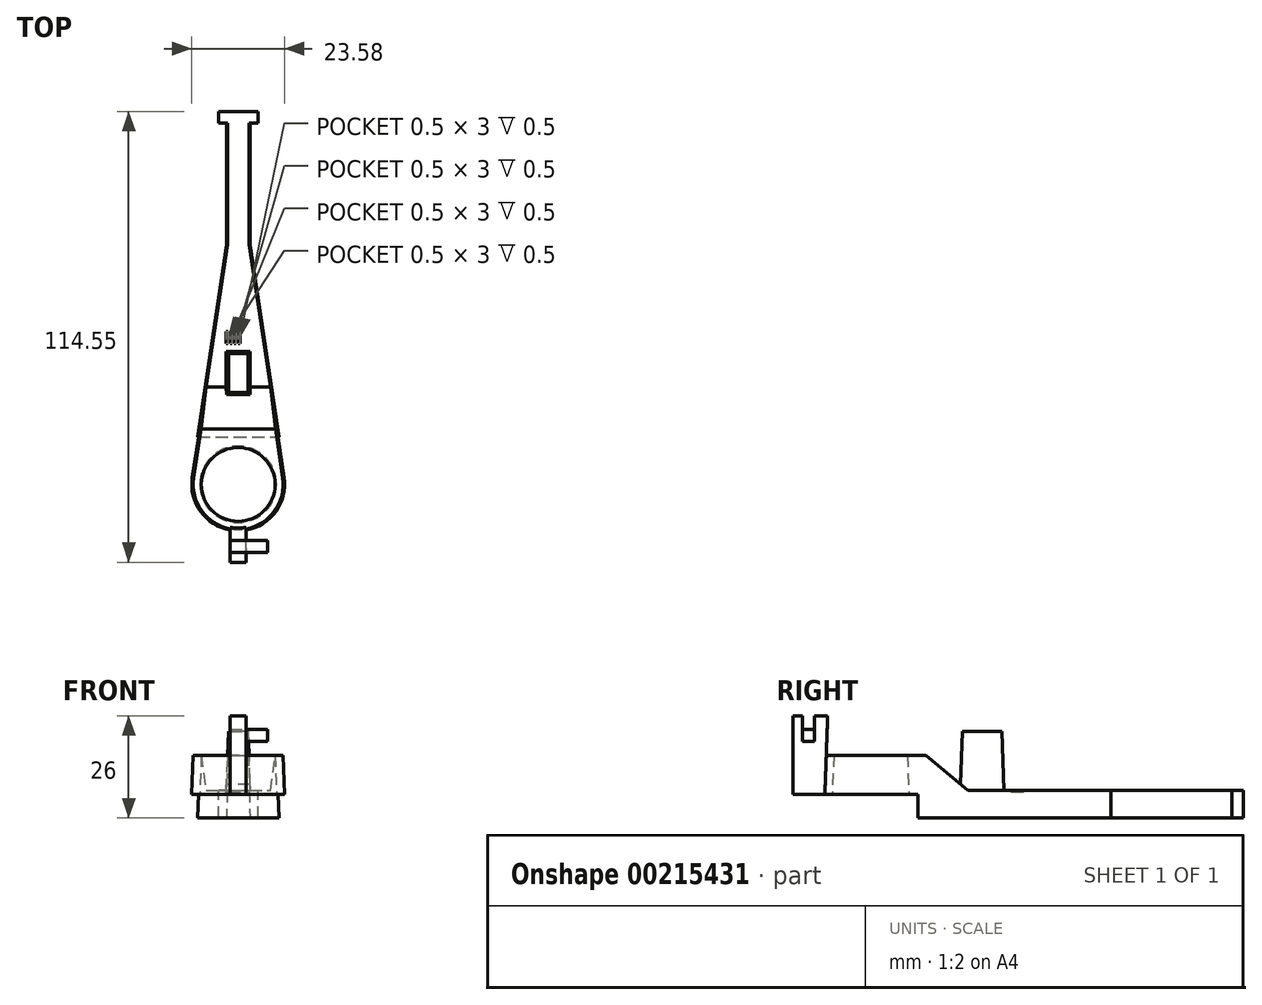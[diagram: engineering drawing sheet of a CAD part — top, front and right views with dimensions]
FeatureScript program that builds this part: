
annotation { "Feature Type Name" : "Feature", "Feature Type Description" : "" }
export const myFeature = defineFeature(function(context is Context, id is Id, definition is map)
    precondition{}
    {
        {
            var Q0;
            Q0=qCreatedBy(makeId("Top.planeOp"),FACE);
            var sketch = newSketch(context, id + "F0", { "sketchPlane" : qUnion([Q0])});
            skCircle(sketch, "E0", {"center": v(0, 0) * mm, "radius": 12 * mm});
            skLineSegment(sketch, "E1", {"start": v(-3, 95) * mm, "end": v(3, 95) * mm});
            skLineSegment(sketch, "E2", {"start": v(0, -12) * mm, "end": v(0, 95) * mm, "construction": true});
            skPoint(sketch, "E3", {"position": v(0, 95) * mm});
            skLineSegment(sketch, "E4", {"start": v(-3, 95) * mm, "end": v(-3, 61) * mm});
            skLineSegment(sketch, "E5", {"start": v(3, 95) * mm, "end": v(3, 61) * mm});
            skLineSegment(sketch, "E6", {"start": v(-3, 61) * mm, "end": v(-11.87, 1.78) * mm});
            skLineSegment(sketch, "E7", {"start": v(3, 61) * mm, "end": v(11.87, 1.78) * mm});
            skSolve(sketch);
        }
        {
            var Q0;
            Q0=qSketchRegion(id+"F0",true);
            extrude(context, id + "F1", {"entities" : qUnion([Q0]), "depth" : 16 * mm, "hasDraft" : true, "draftAngle" : 2 * degree, "draftPullDirection" : true});
        }
        {
            var Q0;
            Q0=qCreatedBy(makeId("Right.planeOp"),FACE);
            cPlane(context, id + "F2", {"entities" : qUnion([Q0]), "cplaneType" : CPlaneType.OFFSET, "offset" : 12 * mm, "width" : 150 * mm, "height" : 150 * mm});
        }
        {
            var Q0;
            Q0=qCreatedBy(id+"F2.planeOp",FACE);
            var sketch = newSketch(context, id + "F3", { "sketchPlane" : qUnion([Q0])});
            skLineSegment(sketch, "E8", {"start": v(94.76, 7) * mm, "end": v(24.76, 7) * mm});
            skLineSegment(sketch, "E9", {"start": v(24.76, 7) * mm, "end": v(14.03, 16) * mm});
            skLineSegment(sketch, "E10", {"start": v(12, 0) * mm, "end": v(12, 6) * mm});
            skLineSegment(sketch, "E11", {"start": v(12, 6) * mm, "end": v(-11.8, 6) * mm});
            skLineSegment(sketch, "E12", {"start": v(12, 0) * mm, "end": v(-12, 0) * mm});
            skLineSegment(sketch, "E13", {"start": v(-12, 0) * mm, "end": v(-11.8, 6) * mm});
            skLineSegment(sketch, "E14", {"start": v(14.03, 16) * mm, "end": v(94.44, 16) * mm});
            skLineSegment(sketch, "E15", {"start": v(94.44, 16) * mm, "end": v(94.76, 7) * mm});
            skSolve(sketch);
        }
        {
            var Q0;
            Q0=qSketchRegion(id+"F3",true);
            extrude(context, id + "F4", {"entities" : qUnion([Q0]), "operationType" : NewBodyOperationType.REMOVE, "endBound" : BoundingType.THROUGH_ALL, "oppositeDirection" : true, "depth" : 25 * mm});
        }
        {
            var Q0;
            Q0=makeQuery(id+"F4.boolean.opBoolean","COPY",FACE,{"derivedFrom":makeQuery(id+"F4.opExtrude","SWEPT_FACE",FACE,{"disambiguationData":[OSD([sQuery(id+"F3.wireOp",EDGE,"E8")])]})});
            cPlane(context, id + "F5", {"entities" : qUnion([Q0]), "cplaneType" : CPlaneType.OFFSET, "offset" : 15 * mm, "width" : 150 * mm, "height" : 150 * mm});
        }
        {
            var Q0;
            Q0=qCreatedBy(id+"F5.planeOp",FACE);
            var sketch = newSketch(context, id + "F6", { "sketchPlane" : qUnion([Q0])});
            skLineSegment(sketch, "E16.bottom", {"start": v(-2.5, 23.3) * mm, "end": v(2.5, 23.3) * mm});
            skLineSegment(sketch, "E16.top", {"start": v(-2.5, 33.3) * mm, "end": v(2.5, 33.3) * mm});
            skLineSegment(sketch, "E16.left", {"start": v(-2.5, 23.3) * mm, "end": v(-2.5, 33.3) * mm});
            skLineSegment(sketch, "E16.right", {"start": v(2.5, 23.3) * mm, "end": v(2.5, 33.3) * mm});
            skPoint(sketch, "E16.middle", {"position": v(0, 28.3) * mm});
            skSolve(sketch);
        }
        {
            var Q0;
            Q0=qSketchRegion(id+"F6",true);
            extrude(context, id + "F7", {"entities" : qUnion([Q0]), "operationType" : NewBodyOperationType.ADD, "endBound" : BoundingType.UP_TO_NEXT, "oppositeDirection" : true, "depth" : 25 * mm, "hasDraft" : true, "draftAngle" : 2 * degree});
        }
        {
            var Q0;
            Q0=makeQuery(id+"F4.boolean.opBoolean","COPY",FACE,{"derivedFrom":makeQuery(id+"F4.opExtrude","SWEPT_FACE",FACE,{"disambiguationData":[OSD([sQuery(id+"F3.wireOp",EDGE,"E11")])]})});
            var sketch = newSketch(context, id + "F8", { "sketchPlane" : qUnion([Q0])});
            skCircle(sketch, "E17", {"center": v(0, 0) * mm, "radius": 9.72 * mm});
            skSolve(sketch);
        }
        {
            var Q0;
            Q0=qSketchRegion(id+"F8",true);
            extrude(context, id + "F9", {"entities" : qUnion([Q0]), "operationType" : NewBodyOperationType.REMOVE, "endBound" : BoundingType.THROUGH_ALL, "oppositeDirection" : true, "depth" : 25 * mm, "hasDraft" : true, "draftAngle" : 2 * degree, "draftPullDirection" : true});
        }
        {
            var Q0;
            Q0=makeQuery(id+"F4.boolean.opBoolean","COPY",FACE,{"derivedFrom":makeQuery(id+"F4.opExtrude","SWEPT_FACE",FACE,{"disambiguationData":[OSD([sQuery(id+"F3.wireOp",EDGE,"E11")])]})});
            var sketch = newSketch(context, id + "F10", { "sketchPlane" : qUnion([Q0])});
            skLineSegment(sketch, "E18", {"start": v(0, 11.8) * mm, "end": v(0, 19.8) * mm, "construction": true});
            skPoint(sketch, "E18.endSnap0", {"position": v(0, 11.8) * mm});
            skLineSegment(sketch, "E19", {"start": v(0, 19.8) * mm, "end": v(-2, 19.8) * mm});
            skLineSegment(sketch, "E20", {"start": v(-2, 19.8) * mm, "end": v(-2, 11.62) * mm});
            skLineSegment(sketch, "E21", {"start": v(0, 19.8) * mm, "end": v(2, 19.8) * mm});
            skLineSegment(sketch, "E22", {"start": v(2, 19.8) * mm, "end": v(2, 11.62) * mm});
            skArc(sketch, "E23", {"start": v(2, 11.62) * mm, "mid": v(0, 11.8) * mm, "end": v(-2, 11.62) * mm});
            skSolve(sketch);
        }
        {
            var Q0;
            Q0=qCreatedBy(makeId("Front.planeOp"),FACE);
            var Q1;
            Q1=sQuery(id+"F10.wireOp",VERTEX,"E21.start");
            cPlane(context, id + "F11", {"entities" : qUnion([Q0, Q1]), "cplaneType" : CPlaneType.PLANE_POINT, "offset" : 25 * mm, "width" : 150 * mm, "height" : 150 * mm});
        }
        {
            var Q0;
            Q0=qCreatedBy(id+"F11.planeOp",FACE);
            var sketch = newSketch(context, id + "F12", { "sketchPlane" : qUnion([Q0])});
            skLineSegment(sketch, "E24.bottom", {"start": v(-2, 6) * mm, "end": v(2, 6) * mm});
            skLineSegment(sketch, "E24.top", {"start": v(-2, 26) * mm, "end": v(2, 26) * mm});
            skLineSegment(sketch, "E24.left", {"start": v(-2, 6) * mm, "end": v(-2, 26) * mm});
            skLineSegment(sketch, "E24.right", {"start": v(2, 6) * mm, "end": v(2, 26) * mm});
            skSolve(sketch);
        }
        {
            var Q0;
            Q0=qSketchRegion(id+"F12",true);
            var Q1;
            Q1=makeQuery(id+"F1.opExtrude","SWEPT_FACE",FACE,{"disambiguationData":[OSD([sQuery(id+"F0.wireOp",EDGE,"E0")])]});
            extrude(context, id + "F13", {"entities" : qUnion([Q0]), "operationType" : NewBodyOperationType.ADD, "endBound" : BoundingType.UP_TO_SURFACE, "oppositeDirection" : true, "endBoundEntityFace" : qUnion([Q1]), "depth" : 8 * mm});
        }
        {
            var Q0;
            Q0=makeQuery(id+"F13.opExtrude","SWEPT_FACE",FACE,{"disambiguationData":[OSD([sQuery(id+"F12.wireOp",EDGE,"E24.right")])]});
            var sketch = newSketch(context, id + "F14", { "sketchPlane" : qUnion([Q0])});
            skLineSegment(sketch, "E25.bottom", {"start": v(-17.3, 22.5) * mm, "end": v(-14.3, 22.5) * mm});
            skLineSegment(sketch, "E25.top", {"start": v(-17.3, 19.5) * mm, "end": v(-14.3, 19.5) * mm});
            skLineSegment(sketch, "E25.left", {"start": v(-17.3, 22.5) * mm, "end": v(-17.3, 19.5) * mm});
            skLineSegment(sketch, "E25.right", {"start": v(-14.3, 22.5) * mm, "end": v(-14.3, 19.5) * mm});
            skSolve(sketch);
        }
        {
            var Q0;
            Q0=qSketchRegion(id+"F14",true);
            extrude(context, id + "F15", {"entities" : qUnion([Q0]), "operationType" : NewBodyOperationType.ADD, "depth" : 5.5 * mm});
        }
        {
            var Q0;
            Q0=makeQuery(id+"F13.opExtrude","SWEPT_FACE",FACE,{"disambiguationData":[OSD([sQuery(id+"F12.wireOp",EDGE,"E24.right")])]});
            var sketch = newSketch(context, id + "F16", { "sketchPlane" : qUnion([Q0])});
            skLineSegment(sketch, "E26.bottom", {"start": v(-17.3, 22.5) * mm, "end": v(-14.3, 22.5) * mm});
            skLineSegment(sketch, "E26.top", {"start": v(-17.3, 26) * mm, "end": v(-14.3, 26) * mm});
            skLineSegment(sketch, "E26.left", {"start": v(-17.3, 22.5) * mm, "end": v(-17.3, 26) * mm});
            skLineSegment(sketch, "E26.right", {"start": v(-14.3, 22.5) * mm, "end": v(-14.3, 26) * mm});
            skSolve(sketch);
        }
        {
            var Q0;
            Q0=qSketchRegion(id+"F16",true);
            extrude(context, id + "F17", {"entities" : qUnion([Q0]), "operationType" : NewBodyOperationType.REMOVE, "endBound" : BoundingType.THROUGH_ALL, "oppositeDirection" : true, "depth" : 25 * mm});
        }
        {
            var Q0;
            Q0=makeQuery(id+"F4.boolean.opBoolean","COPY",FACE,{"derivedFrom":makeQuery(id+"F4.opExtrude","SWEPT_FACE",FACE,{"disambiguationData":[OSD([sQuery(id+"F3.wireOp",EDGE,"E8")])]})});
            var sketch = newSketch(context, id + "F18", { "sketchPlane" : qUnion([Q0])});
            skLineSegment(sketch, "E27.bottom", {"start": v(-3.02, 38.82) * mm, "end": v(-2.52, 38.82) * mm});
            skLineSegment(sketch, "E27.top", {"start": v(-3.02, 35.82) * mm, "end": v(-2.52, 35.82) * mm});
            skLineSegment(sketch, "E27.left", {"start": v(-3.02, 38.82) * mm, "end": v(-3.02, 35.82) * mm});
            skLineSegment(sketch, "E27.right", {"start": v(-2.52, 38.82) * mm, "end": v(-2.52, 35.82) * mm});
            skLineSegment(sketch, "E28.1.0.0", {"start": v(-1.52, 38.82) * mm, "end": v(-1.52, 35.82) * mm});
            skLineSegment(sketch, "E28.1.0.1", {"start": v(-2.02, 38.82) * mm, "end": v(-1.52, 38.82) * mm});
            skLineSegment(sketch, "E28.1.0.2", {"start": v(-2.02, 38.82) * mm, "end": v(-2.02, 35.82) * mm});
            skLineSegment(sketch, "E28.1.0.3", {"start": v(-2.02, 35.82) * mm, "end": v(-1.52, 35.82) * mm});
            skLineSegment(sketch, "E28.2.0.0", {"start": v(-0.52, 38.82) * mm, "end": v(-0.52, 35.82) * mm});
            skLineSegment(sketch, "E28.2.0.1", {"start": v(-1.02, 38.82) * mm, "end": v(-0.52, 38.82) * mm});
            skLineSegment(sketch, "E28.2.0.2", {"start": v(-1.02, 38.82) * mm, "end": v(-1.02, 35.82) * mm});
            skLineSegment(sketch, "E28.2.0.3", {"start": v(-1.02, 35.82) * mm, "end": v(-0.52, 35.82) * mm});
            skLineSegment(sketch, "E28.3.0.0", {"start": v(0.48, 38.82) * mm, "end": v(0.48, 35.82) * mm});
            skLineSegment(sketch, "E28.3.0.1", {"start": v(-0.02, 38.82) * mm, "end": v(0.48, 38.82) * mm});
            skLineSegment(sketch, "E28.3.0.2", {"start": v(-0.02, 38.82) * mm, "end": v(-0.02, 35.82) * mm});
            skLineSegment(sketch, "E28.3.0.3", {"start": v(-0.02, 35.82) * mm, "end": v(0.48, 35.82) * mm});
            skLineSegment(sketch, "E28.direction1", {"start": v(-2.52, 35.82) * mm, "end": v(-1.52, 35.82) * mm, "construction": true});
            skSolve(sketch);
        }
        {
            var Q0;
            Q0=qSketchRegion(id+"F18",true);
            extrude(context, id + "F19", {"entities" : qUnion([Q0]), "operationType" : NewBodyOperationType.REMOVE, "oppositeDirection" : true, "depth" : 0.5 * mm});
        }
        {
            var Q0;
            Q0=makeQuery(id+"F4.boolean.opBoolean","COPY",FACE,{"derivedFrom":makeQuery(id+"F4.opExtrude","SWEPT_FACE",FACE,{"disambiguationData":[OSD([sQuery(id+"F3.wireOp",EDGE,"E8")])]})});
            var sketch = newSketch(context, id + "F20", { "sketchPlane" : qUnion([Q0])});
            skLineSegment(sketch, "E29", {"start": v(0, 95) * mm, "end": v(0, 85) * mm, "construction": true});
            skLineSegment(sketch, "E30", {"start": v(-2, 95) * mm, "end": v(-3, 95) * mm});
            skLineSegment(sketch, "E31", {"start": v(-5, 94.76) * mm, "end": v(-5, 91.76) * mm});
            skLineSegment(sketch, "E32", {"start": v(-5, 91.76) * mm, "end": v(-3, 91.76) * mm});
            skLineSegment(sketch, "E33", {"start": v(-2.76, 94.76) * mm, "end": v(-2.76, 91.76) * mm});
            skLineSegment(sketch, "E34", {"start": v(-2.76, 91.76) * mm, "end": v(-3, 91.76) * mm});
            skLineSegment(sketch, "E35", {"start": v(-2.76, 94.76) * mm, "end": v(0, 94.76) * mm});
            skLineSegment(sketch, "E36", {"start": v(-2, 95) * mm, "end": v(0, 95) * mm});
            skPoint(sketch, "E37.orphan", {"position": v(-3, 95) * mm});
            skLineSegment(sketch, "E38", {"start": v(-2.76, 94.76) * mm, "end": v(-5, 94.76) * mm});
            skLineSegment(sketch, "E39", {"start": v(-3, 95) * mm, "end": v(-3, 94.76) * mm});
            skPoint(sketch, "E40.orphan", {"position": v(-5, 95) * mm});
            skLineSegment(sketch, "E41.MirrorCS", {"start": v(2, 95) * mm, "end": v(0, 95) * mm});
            skLineSegment(sketch, "E42.MirrorCS", {"start": v(2, 95) * mm, "end": v(3, 95) * mm});
            skPoint(sketch, "E43.MirrorP", {"position": v(3, 95) * mm});
            skLineSegment(sketch, "E44.MirrorCS", {"start": v(3, 95) * mm, "end": v(3, 94.76) * mm});
            skLineSegment(sketch, "E45.MirrorCS", {"start": v(2.76, 94.76) * mm, "end": v(0, 94.76) * mm});
            skLineSegment(sketch, "E46.MirrorCS", {"start": v(2.76, 94.76) * mm, "end": v(5, 94.76) * mm});
            skLineSegment(sketch, "E47.MirrorCS", {"start": v(2.76, 94.76) * mm, "end": v(2.76, 91.76) * mm});
            skLineSegment(sketch, "E48.MirrorCS", {"start": v(5, 91.76) * mm, "end": v(3, 91.76) * mm});
            skLineSegment(sketch, "E49.MirrorCS", {"start": v(5, 94.76) * mm, "end": v(5, 91.76) * mm});
            skLineSegment(sketch, "E50.MirrorCS", {"start": v(2.76, 91.76) * mm, "end": v(3, 91.76) * mm});
            skSolve(sketch);
        }
        {
            var Q0;
            Q0=makeQuery(id+"F20.imprint","IMPRINT",FACE,{"disambiguationData":[TD([[makeQuery(id+"F20.imprint","IMPRINT",EDGE,{"derivedFrom":sQuery(id+"F20.wireOp",EDGE,"E30")}),1.0]])]});
            extrude(context, id + "F21", {"entities" : qUnion([Q0]), "operationType" : NewBodyOperationType.REMOVE, "endBound" : BoundingType.THROUGH_ALL, "oppositeDirection" : true, "depth" : 25 * mm});
        }
        {
            var Q0;
            {var subQ1=sQuery(id+"F20.wireOp",EDGE,"E31");Q0=makeQuery(id+"F20.imprint","IMPRINT",FACE,{"disambiguationData":[TD([[makeQuery(id+"F20.imprint","IMPRINT",EDGE,{"derivedFrom":subQ1}),1.0]])]});}
            var Q1;
            {var subQ3=sQuery(id+"F20.wireOp",EDGE,"E47.MirrorCS");Q1=makeQuery(id+"F20.imprint","IMPRINT",FACE,{"disambiguationData":[TD([[makeQuery(id+"F20.imprint","IMPRINT",EDGE,{"derivedFrom":subQ3}),1.0]])]});}
            var Q2;
            Q2=makeQuery(id+"F1.opExtrude","CAP_FACE",FACE,{"disambiguationData":[OSD([sQuery(id+"F0.wireOp",EDGE,"E0"),sQuery(id+"F0.wireOp",EDGE,"E1"),sQuery(id+"F0.wireOp",EDGE,"E4"),sQuery(id+"F0.wireOp",EDGE,"E5"),sQuery(id+"F0.wireOp",EDGE,"E6"),sQuery(id+"F0.wireOp",EDGE,"E7")])],"isStart":true});
            extrude(context, id + "F22", {"entities" : qUnion([Q0, Q1]), "operationType" : NewBodyOperationType.ADD, "endBound" : BoundingType.UP_TO_SURFACE, "oppositeDirection" : true, "endBoundEntityFace" : qUnion([Q2]), "depth" : 25 * mm});
        }
    });
